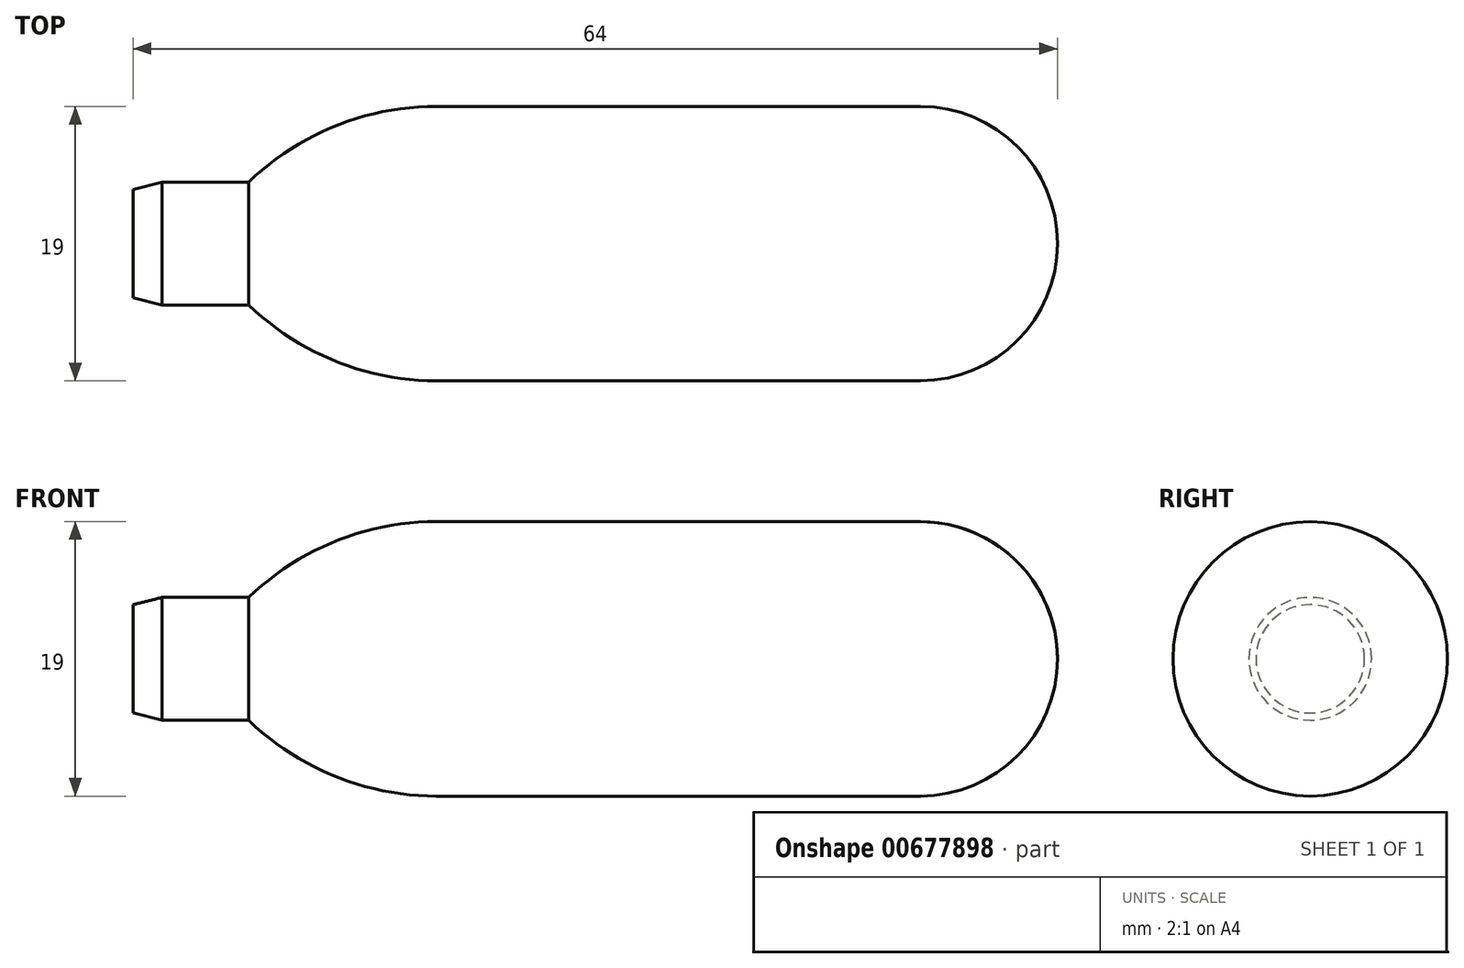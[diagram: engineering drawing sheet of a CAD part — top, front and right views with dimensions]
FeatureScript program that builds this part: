
annotation { "Feature Type Name" : "Feature", "Feature Type Description" : "" }
export const myFeature = defineFeature(function(context is Context, id is Id, definition is map)
    precondition{}
    {
        {
            var Q0;
            Q0=qCreatedBy(makeId("Front.planeOp"),FACE);
            var sketch = newSketch(context, id + "F0", { "sketchPlane" : qUnion([Q0])});
            skLineSegment(sketch, "E0", {"start": v(0, 0) * mm, "end": v(64, 0) * mm});
            skLineSegment(sketch, "E1", {"start": v(54.5, 0) * mm, "end": v(64, 0) * mm});
            skArc(sketch, "E2", {"start": v(64, 0) * mm, "mid": v(61.22, 6.72) * mm, "end": v(54.5, 9.5) * mm});
            skLineSegment(sketch, "E3", {"start": v(0, 0) * mm, "end": v(0, 3.75) * mm});
            skLineSegment(sketch, "E4", {"start": v(0, 3.75) * mm, "end": v(2, 4.25) * mm});
            skLineSegment(sketch, "E5", {"start": v(2, 4.25) * mm, "end": v(8, 4.25) * mm});
            skLineSegment(sketch, "E6", {"start": v(54.5, 9.5) * mm, "end": v(21, 9.5) * mm});
            skArc(sketch, "E7", {"start": v(21, 9.5) * mm, "mid": v(13.99, 8.14) * mm, "end": v(8, 4.25) * mm});
            skSolve(sketch);
        }
        {
            var Q0;
            Q0=makeQuery(id+"F0.imprint","IMPRINT",FACE,{"disambiguationData":[TD([[makeQuery(id+"F0.imprint","IMPRINT",EDGE,{"derivedFrom":sQuery(id+"F0.wireOp",EDGE,"E0")}),1.0]])]});
            var Q1;
            Q1=sQuery(id+"F0.wireOp",EDGE,"E0");
            revolve(context, id + "F1", {"entities" : qUnion([Q0]), "axis" : qUnion([Q1]), "revolveType" : RevolveType.FULL});
        }
    });
